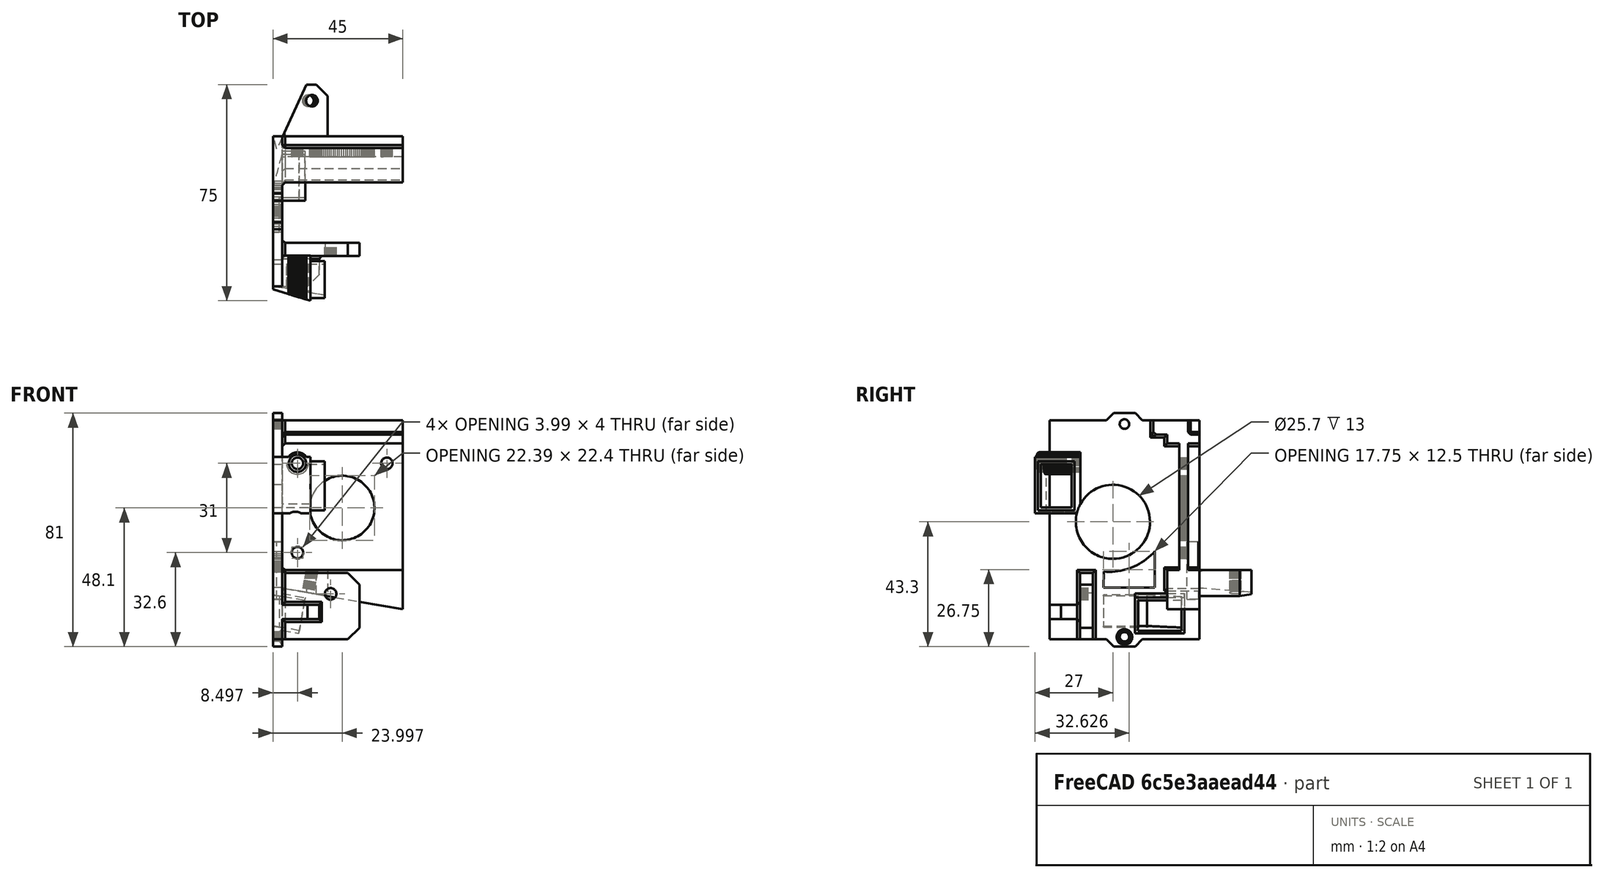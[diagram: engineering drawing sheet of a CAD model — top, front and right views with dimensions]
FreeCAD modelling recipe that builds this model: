
FCSTD DOCUMENT  (FreeCAD 0.20R29410 (Git))
Label: BMG_plate_bigger_hole
License: All rights reserved
LicenseURL: http://en.wikipedia.org/wiki/All_rights_reserved
objects: Part::RuledSurface×5, Part::Feature×3, Part::Plane×3, Part::MultiFuse×3, Part::FeaturePython×3, Part::Cylinder×2, Part::Extrusion×2, Part::Cut×2, Sketcher::SketchObject×1, Part::Compound×1, Part::Refine×1, App::DocumentObjectGroup×1
note: 26 computed .brp shape members not serialized (recipe doc carries the construction recipe); baked Part::Feature solids carry a one-line shape summary decoded from their .brp

FEATURE [Part::Cylinder] Cylinder
  Angle = 360
  AttacherType = Attacher::AttachEngine3D
  FirstAngle = 0
  Height = 50
  Placement = pos=(0,-4,-87.2) rot=(0,1,0;1.5708rad)
  Radius = 12.85
  SecondAngle = 0
FEATURE [Part::Feature] DirectDrivePlate001001001
  shape: bbox 45 x 75 x 81 mm, 1170 faces, 0 solids (baked)
FEATURE [Part::Feature] DirectDrivePlate001001001_solid  label="DirectDrivePlate001001001 (Solid)"
  shape: bbox 45 x 75 x 81 mm, 1170 faces (baked)
FEATURE [Part::Cylinder] Cylinder001
  Angle = 360
  AttacherType = Attacher::AttachEngine3D
  FirstAngle = 0
  Height = 4
  Placement = pos=(3,0,-127.2) rot=(0,1,0;1.5708rad)
  Radius = 2.7
  SecondAngle = 0
FEATURE [Part::Plane] Plane
  AttacherType = Attacher::AttachEngine3D
  Length = 10
  Placement = pos=(-0.7,32.2,-114.1) rot=(0,0,1;0rad)
  Width = 10
FEATURE [Sketcher::SketchObject] Sketch
  FullyConstrained = false
  MapMode = 5
  Placement = pos=(-0.7,32.2,-114.1) rot=(0,0,1;0rad)
  Support = -> [Plane]
  sketch-geometry (3):
    g0: LineSegment StartX=12.7413 StartY=12.7444 StartZ=0 EndX=2.07192 EndY=-10.5623 EndZ=0
    g1: LineSegment StartX=2.07192 StartY=-10.5623 StartZ=0 EndX=-3.75578 EndY=11.4672 EndZ=0
    g2: LineSegment StartX=-3.75578 StartY=11.4672 StartZ=0 EndX=12.7413 EndY=12.7444 EndZ=0
  constraints (3):
    c: Coincident(g1,g0)
    c: Coincident(g2,g1)
    c: Coincident(g2,g0)
FEATURE [Part::Extrusion] Extrude
  Base = -> Sketch
  Dir = (0,0,1)
  DirMode = 2
  FaceMakerClass = Part::FaceMakerBullseye
  LengthFwd = 20
  LengthRev = 0
  Solid = true
  Symmetric = false
FEATURE [Part::MultiFuse] Fusion
  Shapes = -> [Cylinder,Cylinder001,Extrude]
FEATURE [Part::Plane] Plane001
  AttacherType = Attacher::AttachEngine3D
  Length = 20
  Placement = pos=(3.2,-9.6,-130.5) rot=(0,1,0;4.71239rad)
  Width = 20
FEATURE [Part::FeaturePython] Slice  # WARN: FeaturePython — macro-defined, semantics opaque (R4)
  Base = -> DirectDrivePlate001001001_solid
  Mode = 1
  Tolerance = 0
  Tools = -> [Plane001]
FEATURE [Part::FeaturePython] Slice_child0  label="Slice.0"  # WARN: FeaturePython — macro-defined, semantics opaque (R4)
  Base = -> Slice
  FilterType = 1
  Invert = false
  OverrideMaxVal = 0
  WindowFrom = 80
  WindowTo = 100
  items = 0
FEATURE [Part::FeaturePython] Slice_child1  label="Slice.1"  # WARN: FeaturePython — macro-defined, semantics opaque (R4)
  Base = -> Slice
  FilterType = 1
  Invert = false
  OverrideMaxVal = 0
  Placement = pos=(0,12,0) rot=(0,0,1;0rad)
  WindowFrom = 80
  WindowTo = 100
  items = 1
FEATURE [Part::Plane] Plane002
  AttacherType = Attacher::AttachEngine3D
  Length = 14
  Placement = pos=(3.2,-9.6,-124.5) rot=(0,-1,0;1.5708rad)
  Width = 14.4
FEATURE [Part::Extrusion] Extrude001
  Base = -> Plane002
  Dir = (-1,0,2e-16)
  DirMode = 2
  FaceMakerClass = Part::FaceMakerBullseye
  LengthFwd = 1
  LengthRev = 0
  Solid = false
  Symmetric = false
FEATURE [Part::MultiFuse] Fusion001
  Shapes = -> [Extrude001,Slice_child0]
FEATURE [Part::Cut] Cut  label="BMG plate"
  Base = -> Fusion001
  Tool = -> Fusion
FEATURE [Part::RuledSurface] Ruled_Surface
  Curve1 = -> Cut [Edge750]
  Curve2 = -> Slice_child1 [Edge11]
  Orientation = 0
FEATURE [Part::RuledSurface] Ruled_Surface001
  Curve1 = -> Cut [Edge180]
  Curve2 = -> Cut [Edge750]
  Orientation = 0
FEATURE [Part::RuledSurface] Ruled_Surface002
  Curve1 = -> Ruled_Surface [Edge3]
  Curve2 = -> Ruled_Surface001 [Edge1]
  Orientation = 0
FEATURE [Part::RuledSurface] Ruled_Surface003
  Curve1 = -> Ruled_Surface [Edge4]
  Curve2 = -> Ruled_Surface002 [Edge2]
  Orientation = 0
FEATURE [Part::RuledSurface] Ruled_Surface004
  Curve1 = -> Ruled_Surface002 [Edge4]
  Curve2 = -> Ruled_Surface [Edge2]
  Orientation = 0
FEATURE [Part::Compound] Compound
  Links = -> [Ruled_Surface002,Ruled_Surface,Ruled_Surface001,Ruled_Surface004,Ruled_Surface003]
FEATURE [Part::Refine] Compound001
  Source = -> Compound
FEATURE [Part::Feature] Compound001_solid  label="Compound001 (Solid)"
  shape: bbox 3.2 x 12 x 11.36 mm, 5 faces (baked)
FEATURE [Part::Cut] Cut001
  Base = -> Cut
  Tool = -> Compound001_solid
FEATURE [Part::MultiFuse] Fusion002
  Shapes = -> [Slice_child1,Cut001]
FEATURE [App::DocumentObjectGroup] GrExplode_Slice  label="Exploded Slice"
  Group = -> [Slice_child0,Fusion002]
